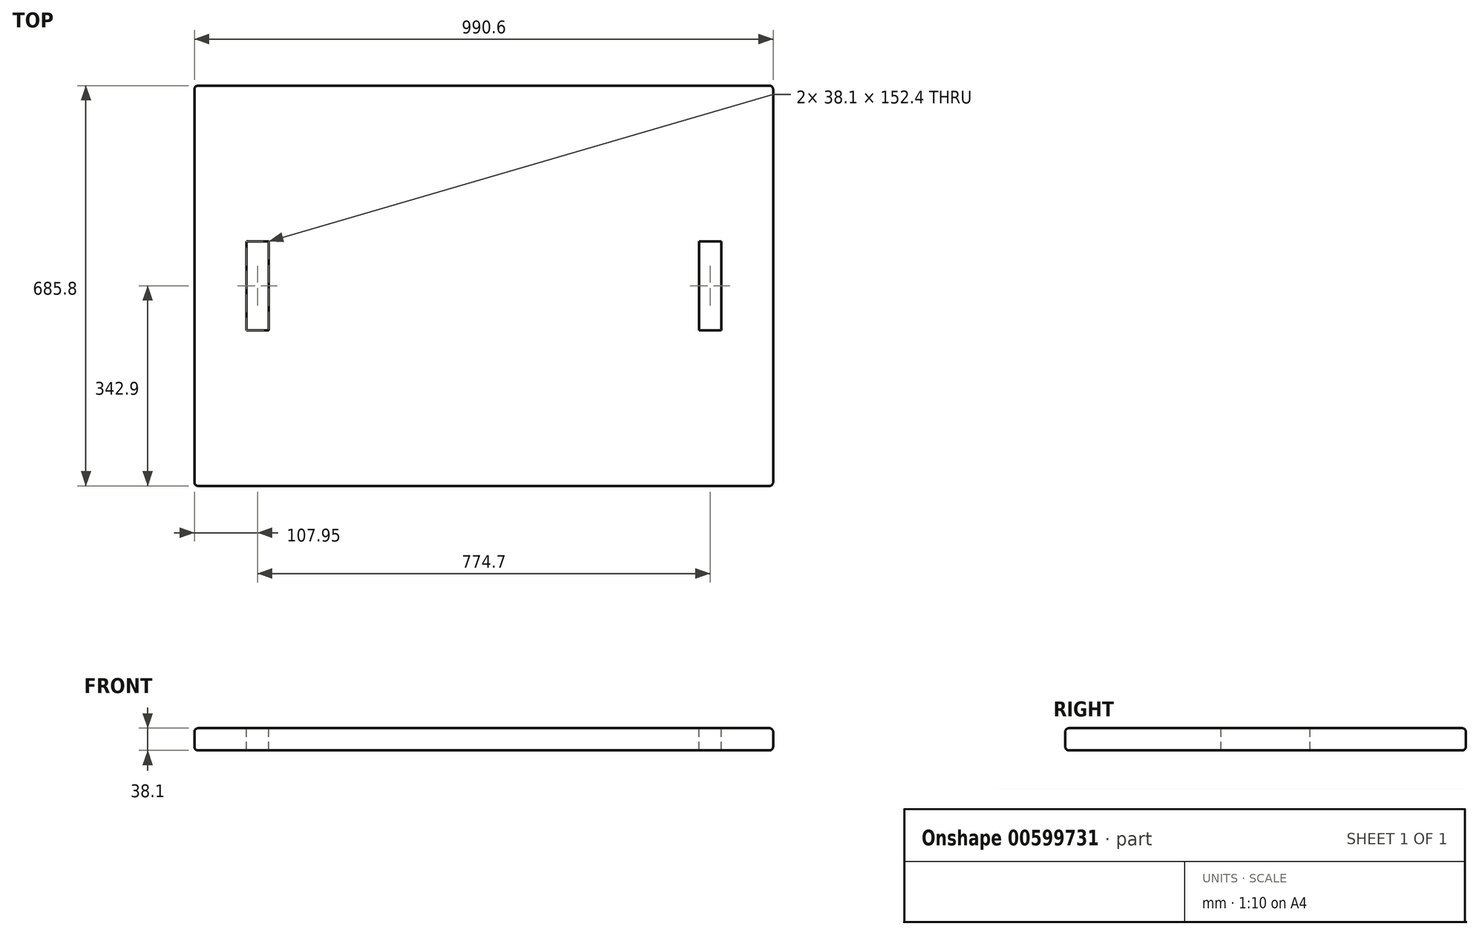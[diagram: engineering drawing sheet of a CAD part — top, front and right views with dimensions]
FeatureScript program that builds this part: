
annotation { "Feature Type Name" : "Feature", "Feature Type Description" : "" }
export const myFeature = defineFeature(function(context is Context, id is Id, definition is map)
    precondition{}
    {
        {
            var Q0;
            Q0=qCreatedBy(makeId("Top.planeOp"),FACE);
            var sketch = newSketch(context, id + "F0", { "sketchPlane" : qUnion([Q0])});
            skLineSegment(sketch, "E0.bottom", {"start": v(0, 0) * mm, "end": v(990.6, 0) * mm});
            skLineSegment(sketch, "E0.top", {"start": v(0, 685.8) * mm, "end": v(990.6, 685.8) * mm});
            skLineSegment(sketch, "E0.left", {"start": v(0, 0) * mm, "end": v(0, 685.8) * mm});
            skLineSegment(sketch, "E0.right", {"start": v(990.6, 0) * mm, "end": v(990.6, 685.8) * mm});
            skSolve(sketch);
        }
        {
            var Q0;
            Q0=makeQuery(id+"F0.imprint","IMPRINT",FACE,{"disambiguationData":[TD([[makeQuery(id+"F0.imprint","IMPRINT",EDGE,{"derivedFrom":sQuery(id+"F0.wireOp",EDGE,"E0.bottom")}),1.0]])]});
            extrude(context, id + "F1", {"entities" : qUnion([Q0]), "depth" : 38.1 * mm, "offsetDistance" : 25.4 * mm});
        }
        {
            var Q0;
            Q0=makeQuery(id+"F1.opExtrude","CAP_FACE",FACE,{"disambiguationData":[OSD([sQuery(id+"F0.wireOp",EDGE,"E0.bottom"),sQuery(id+"F0.wireOp",EDGE,"E0.top"),sQuery(id+"F0.wireOp",EDGE,"E0.left"),sQuery(id+"F0.wireOp",EDGE,"E0.right")])],"isStart":false});
            var Q1;
            Q1=makeQuery(id+"F1.opExtrude","CAP_FACE",FACE,{"disambiguationData":[OSD([sQuery(id+"F0.wireOp",EDGE,"E0.bottom"),sQuery(id+"F0.wireOp",EDGE,"E0.top"),sQuery(id+"F0.wireOp",EDGE,"E0.left"),sQuery(id+"F0.wireOp",EDGE,"E0.right")])],"isStart":true});
            var Q2;
            Q2=makeQuery(id+"F1.opExtrude","SWEPT_EDGE",EDGE,{"disambiguationData":[OSD([sQuery(id+"F0.wireOp",EDGE,"E0.bottom"),sQuery(id+"F0.wireOp",EDGE,"E0.left")])]});
            var Q3;
            Q3=makeQuery(id+"F1.opExtrude","SWEPT_EDGE",EDGE,{"disambiguationData":[OSD([sQuery(id+"F0.wireOp",EDGE,"E0.bottom"),sQuery(id+"F0.wireOp",EDGE,"E0.right")])]});
            var Q4;
            Q4=makeQuery(id+"F1.opExtrude","SWEPT_EDGE",EDGE,{"disambiguationData":[OSD([sQuery(id+"F0.wireOp",EDGE,"E0.top"),sQuery(id+"F0.wireOp",EDGE,"E0.right")])]});
            var Q5;
            Q5=makeQuery(id+"F1.opExtrude","SWEPT_EDGE",EDGE,{"disambiguationData":[OSD([sQuery(id+"F0.wireOp",EDGE,"E0.top"),sQuery(id+"F0.wireOp",EDGE,"E0.left")])]});
            fillet(context, id + "F2", {"entities" : qUnion([Q0, Q1, Q2, Q3, Q4, Q5]), "radius" : 6.35 * mm, "tangentPropagation" : true, "allowEdgeOverflow" : false});
        }
        {
            var Q0;
            Q0=makeQuery(id+"F1.opExtrude","CAP_FACE",FACE,{"disambiguationData":[OSD([sQuery(id+"F0.wireOp",EDGE,"E0.bottom"),sQuery(id+"F0.wireOp",EDGE,"E0.top"),sQuery(id+"F0.wireOp",EDGE,"E0.left"),sQuery(id+"F0.wireOp",EDGE,"E0.right")])],"isStart":false});
            var sketch = newSketch(context, id + "F3", { "sketchPlane" : qUnion([Q0])});
            skLineSegment(sketch, "E1.bottom", {"start": v(88.9, 419.1) * mm, "end": v(127, 419.1) * mm});
            skLineSegment(sketch, "E1.top", {"start": v(88.9, 266.7) * mm, "end": v(127, 266.7) * mm});
            skLineSegment(sketch, "E1.left", {"start": v(88.9, 419.1) * mm, "end": v(88.9, 266.7) * mm});
            skLineSegment(sketch, "E1.right", {"start": v(127, 419.1) * mm, "end": v(127, 266.7) * mm});
            skLineSegment(sketch, "E2.bottom", {"start": v(863.6, 419.1) * mm, "end": v(901.7, 419.1) * mm});
            skLineSegment(sketch, "E2.top", {"start": v(863.6, 266.7) * mm, "end": v(901.7, 266.7) * mm});
            skLineSegment(sketch, "E2.left", {"start": v(863.6, 419.1) * mm, "end": v(863.6, 266.7) * mm});
            skLineSegment(sketch, "E2.right", {"start": v(901.7, 419.1) * mm, "end": v(901.7, 266.7) * mm});
            skSolve(sketch);
        }
        {
            var Q0;
            Q0=makeQuery(id+"F3.imprint","IMPRINT",FACE,{"disambiguationData":[TD([[makeQuery(id+"F3.imprint","IMPRINT",EDGE,{"derivedFrom":sQuery(id+"F3.wireOp",EDGE,"E1.bottom")}),-1.0]])]});
            var Q1;
            Q1=makeQuery(id+"F3.imprint","IMPRINT",FACE,{"disambiguationData":[TD([[makeQuery(id+"F3.imprint","IMPRINT",EDGE,{"derivedFrom":sQuery(id+"F3.wireOp",EDGE,"E2.bottom")}),-1.0]])]});
            extrude(context, id + "F4", {"entities" : qUnion([Q0, Q1]), "operationType" : NewBodyOperationType.REMOVE, "endBound" : BoundingType.UP_TO_NEXT, "oppositeDirection" : true, "depth" : 25.4 * mm, "offsetDistance" : 25.4 * mm});
        }
    });
